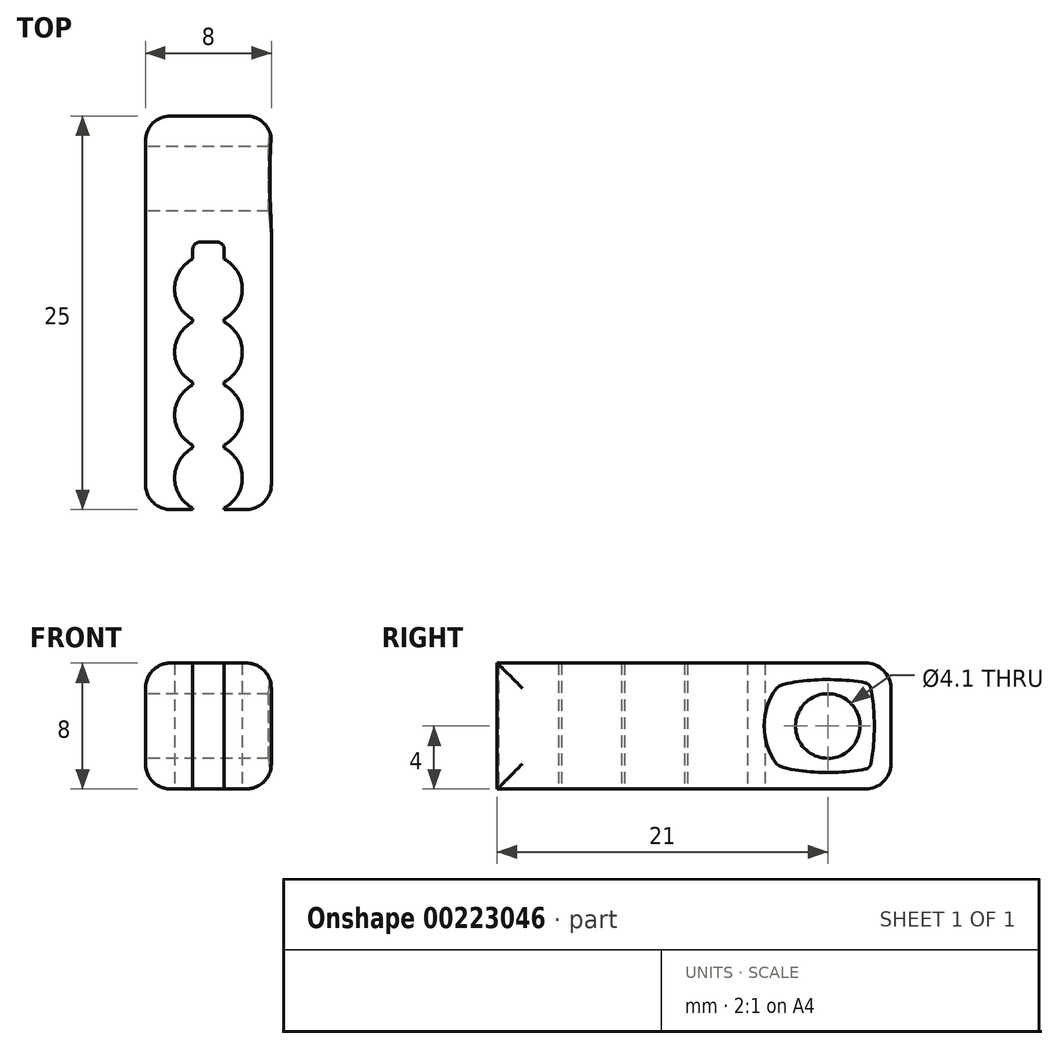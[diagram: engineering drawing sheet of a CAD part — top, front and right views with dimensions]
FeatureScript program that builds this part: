
annotation { "Feature Type Name" : "Feature", "Feature Type Description" : "" }
export const myFeature = defineFeature(function(context is Context, id is Id, definition is map)
    precondition{}
    {
        {
            var Q0;
            Q0=qCreatedBy(makeId("Top.planeOp"),FACE);
            var sketch = newSketch(context, id + "F0", { "sketchPlane" : qUnion([Q0])});
            skLineSegment(sketch, "E0.bottom", {"start": v(4, -4) * mm, "end": v(-4, -4) * mm});
            skLineSegment(sketch, "E0.top", {"start": v(4, 4) * mm, "end": v(-4, 4) * mm});
            skLineSegment(sketch, "E0.left", {"start": v(4, -4) * mm, "end": v(4, 4) * mm});
            skLineSegment(sketch, "E0.right", {"start": v(-4, -4) * mm, "end": v(-4, 4) * mm});
            skPoint(sketch, "E0.middle", {"position": v(0, 0) * mm});
            skLineSegment(sketch, "E1", {"start": v(-4, -4) * mm, "end": v(-4, -21) * mm});
            skLineSegment(sketch, "E2", {"start": v(4, -4) * mm, "end": v(4, -21) * mm});
            skLineSegment(sketch, "E3", {"start": v(4, -21) * mm, "end": v(1, -21) * mm});
            skLineSegment(sketch, "E4", {"start": v(-4, -21) * mm, "end": v(-1, -21) * mm});
            skLineSegment(sketch, "E5", {"start": v(-1, -21) * mm, "end": v(-1, -4) * mm});
            skLineSegment(sketch, "E6", {"start": v(1, -21) * mm, "end": v(1, -4) * mm});
            skLineSegment(sketch, "E7", {"start": v(0, -4) * mm, "end": v(0, -20.2) * mm, "construction": true});
            skCircle(sketch, "E8", {"center": v(0, -19) * mm, "radius": 2.15 * mm});
            skCircle(sketch, "E9.1.0.0", {"center": v(0, -15) * mm, "radius": 2.15 * mm});
            skLineSegment(sketch, "E9.1.0.1", {"start": v(0, 0) * mm, "end": v(0, -16.2) * mm, "construction": true});
            skCircle(sketch, "E9.2.0.0", {"center": v(0, -11) * mm, "radius": 2.15 * mm});
            skLineSegment(sketch, "E9.2.0.1", {"start": v(0, 4) * mm, "end": v(0, -12.2) * mm, "construction": true});
            skCircle(sketch, "E9.3.0.0", {"center": v(0, -7) * mm, "radius": 2.15 * mm});
            skLineSegment(sketch, "E9.3.0.1", {"start": v(0, 8) * mm, "end": v(0, -8.2) * mm, "construction": true});
            skLineSegment(sketch, "E9.direction1", {"start": v(0, -19) * mm, "end": v(0, -15) * mm, "construction": true});
            skSolve(sketch);
        }
        {
            var Q0;
            Q0=makeQuery(id+"F0.imprint","IMPRINT",FACE,{"disambiguationData":[TD([[makeQuery(id+"F0.imprint","IMPRINT",EDGE,{"derivedFrom":sQuery(id+"F0.wireOp",EDGE,"E0.top")}),1.0]])]});
            var Q1;
            {var subQ1=sQuery(id+"F0.wireOp",EDGE,"E1");Q1=makeQuery(id+"F0.imprint","IMPRINT",FACE,{"disambiguationData":[TD([[makeQuery(id+"F0.imprint","IMPRINT",EDGE,{"derivedFrom":subQ1}),1.0]])]});}
            var Q2;
            {var subQ5=sQuery(id+"F0.wireOp",EDGE,"E2");Q2=makeQuery(id+"F0.imprint","IMPRINT",FACE,{"disambiguationData":[TD([[makeQuery(id+"F0.imprint","IMPRINT",EDGE,{"derivedFrom":subQ5}),-1.0]])]});}
            extrude(context, id + "F1", {"entities" : qUnion([Q0, Q1, Q2]), "depth" : 8 * mm});
        }
        {
            var Q0;
            Q0=makeQuery(id+"F1.opExtrude","SWEPT_FACE",FACE,{"disambiguationData":[OSD([sQuery(id+"F0.wireOp",EDGE,"E0.right"),sQuery(id+"F0.wireOp",EDGE,"E1")])]});
            var sketch = newSketch(context, id + "F2", { "sketchPlane" : qUnion([Q0])});
            skCircle(sketch, "E10", {"center": v(0, 4) * mm, "radius": 2.05 * mm});
            skSolve(sketch);
        }
        {
            var Q0;
            Q0=makeQuery(id+"F2.imprint","IMPRINT",FACE,{"disambiguationData":[TD([[makeQuery(id+"F2.imprint","IMPRINT",EDGE,{"derivedFrom":sQuery(id+"F2.wireOp",EDGE,"E10")}),1.0]])]});
            extrude(context, id + "F3", {"entities" : qUnion([Q0]), "operationType" : NewBodyOperationType.REMOVE, "endBound" : BoundingType.THROUGH_ALL, "oppositeDirection" : true, "depth" : 25 * mm});
        }
        {
            var Q0;
            Q0=makeQuery(id+"F1.opExtrude","CAP_EDGE",EDGE,{"disambiguationData":[OSD([sQuery(id+"F0.wireOp",EDGE,"E0.left"),sQuery(id+"F0.wireOp",EDGE,"E2")])],"isStart":false});
            var Q1;
            Q1=makeQuery(id+"F1.opExtrude","CAP_EDGE",EDGE,{"disambiguationData":[OSD([sQuery(id+"F0.wireOp",EDGE,"E0.left"),sQuery(id+"F0.wireOp",EDGE,"E2")])],"isStart":true});
            var Q2;
            Q2=makeQuery(id+"F1.opExtrude","SWEPT_EDGE",EDGE,{"disambiguationData":[OSD([sQuery(id+"F0.wireOp",EDGE,"E0.top"),sQuery(id+"F0.wireOp",EDGE,"E0.left")])]});
            var Q3;
            Q3=makeQuery(id+"F1.opExtrude","SWEPT_EDGE",EDGE,{"disambiguationData":[OSD([sQuery(id+"F0.wireOp",EDGE,"E2"),sQuery(id+"F0.wireOp",EDGE,"E3")])]});
            var Q4;
            Q4=makeQuery(id+"F1.opExtrude","SWEPT_EDGE",EDGE,{"disambiguationData":[OSD([sQuery(id+"F0.wireOp",EDGE,"E1"),sQuery(id+"F0.wireOp",EDGE,"E4")])]});
            var Q5;
            Q5=makeQuery(id+"F1.opExtrude","CAP_EDGE",EDGE,{"disambiguationData":[OSD([sQuery(id+"F0.wireOp",EDGE,"E0.right"),sQuery(id+"F0.wireOp",EDGE,"E1")])],"isStart":false});
            var Q6;
            Q6=makeQuery(id+"F1.opExtrude","CAP_EDGE",EDGE,{"disambiguationData":[OSD([sQuery(id+"F0.wireOp",EDGE,"E0.right"),sQuery(id+"F0.wireOp",EDGE,"E1")])],"isStart":true});
            var Q7;
            Q7=makeQuery(id+"F1.opExtrude","SWEPT_EDGE",EDGE,{"disambiguationData":[OSD([sQuery(id+"F0.wireOp",EDGE,"E0.top"),sQuery(id+"F0.wireOp",EDGE,"E0.right")])]});
            var Q8;
            Q8=makeQuery(id+"F1.opExtrude","CAP_EDGE",EDGE,{"disambiguationData":[OSD([sQuery(id+"F0.wireOp",EDGE,"E0.top")])],"isStart":false});
            var Q9;
            Q9=makeQuery(id+"F1.opExtrude","CAP_EDGE",EDGE,{"disambiguationData":[OSD([sQuery(id+"F0.wireOp",EDGE,"E0.top")])],"isStart":true});
            fillet(context, id + "F4", {"entities" : qUnion([Q0, Q1, Q2, Q3, Q4, Q5, Q6, Q7, Q8, Q9]), "radius" : 1.6 * mm, "tangentPropagation" : true, "allowEdgeOverflow" : false});
        }
        {
            var Q0;
            Q0=makeQuery(id+"F1.opExtrude","SWEPT_EDGE",EDGE,{"disambiguationData":[OSD([sQuery(id+"F0.wireOp",EDGE,"E0.bottom"),sQuery(id+"F0.wireOp",EDGE,"E6")])]});
            var Q1;
            Q1=makeQuery(id+"F1.opExtrude","SWEPT_EDGE",EDGE,{"disambiguationData":[OSD([sQuery(id+"F0.wireOp",EDGE,"E0.bottom"),sQuery(id+"F0.wireOp",EDGE,"E5")])]});
            fillet(context, id + "F5", {"entities" : qUnion([Q0, Q1]), "radius" : 0.5 * mm, "tangentPropagation" : true, "allowEdgeOverflow" : false});
        }
        {
            var Q0;
            Q0=makeQuery(id+"F3.boolean.opBoolean","COPY",EDGE,{"derivedFrom":makeQuery(id+"F3.opExtrude","CAP_EDGE",EDGE,{"disambiguationData":[OSD([sQuery(id+"F2.wireOp",EDGE,"E10")])],"isStart":true})});
            var Q1;
            Q1=makeQuery(id+"F3.boolean.opBoolean","INTERSECT",EDGE,{"derivedFrom":[makeQuery(id+"F1.opExtrude","SWEPT_FACE",FACE,{"disambiguationData":[OSD([sQuery(id+"F0.wireOp",EDGE,"E0.left"),sQuery(id+"F0.wireOp",EDGE,"E2")])]}),makeQuery(id+"F3.opExtrude","SWEPT_FACE",FACE,{"disambiguationData":[OSD([sQuery(id+"F2.wireOp",EDGE,"E10")])]})]});
            chamfer(context, id + "F6", {"entities" : qUnion([Q0, Q1]), "chamferType" : ChamferType.OFFSET_ANGLE, "width" : 2 * mm, "oppositeDirection" : false, "angle" : 5 * degree, "tangentPropagation" : true});
        }
    });
